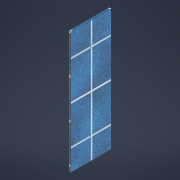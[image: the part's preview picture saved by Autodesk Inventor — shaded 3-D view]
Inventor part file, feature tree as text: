
AUTODESK INVENTOR PART (.ipt)
format: ipt  version: 2022 (Build 260153000, 153)  size: 122,368 bytes
history: native  units: mm
features: extrude x1, sketch x1
ambient origin geometry x8: Origin, YZ Plane, XZ Plane, XY Plane, X Axis, Y Axis, Z Axis, Center Point
bodies: Solid1 (feature_tree)
feature tree (2):
  extrude  "Extrusion1"  Depth=40.0mm
  sketch  "Sketch1"  dims[d0=120.0mm d1=40.0mm d2=2.0mm d3=0.0mm]
